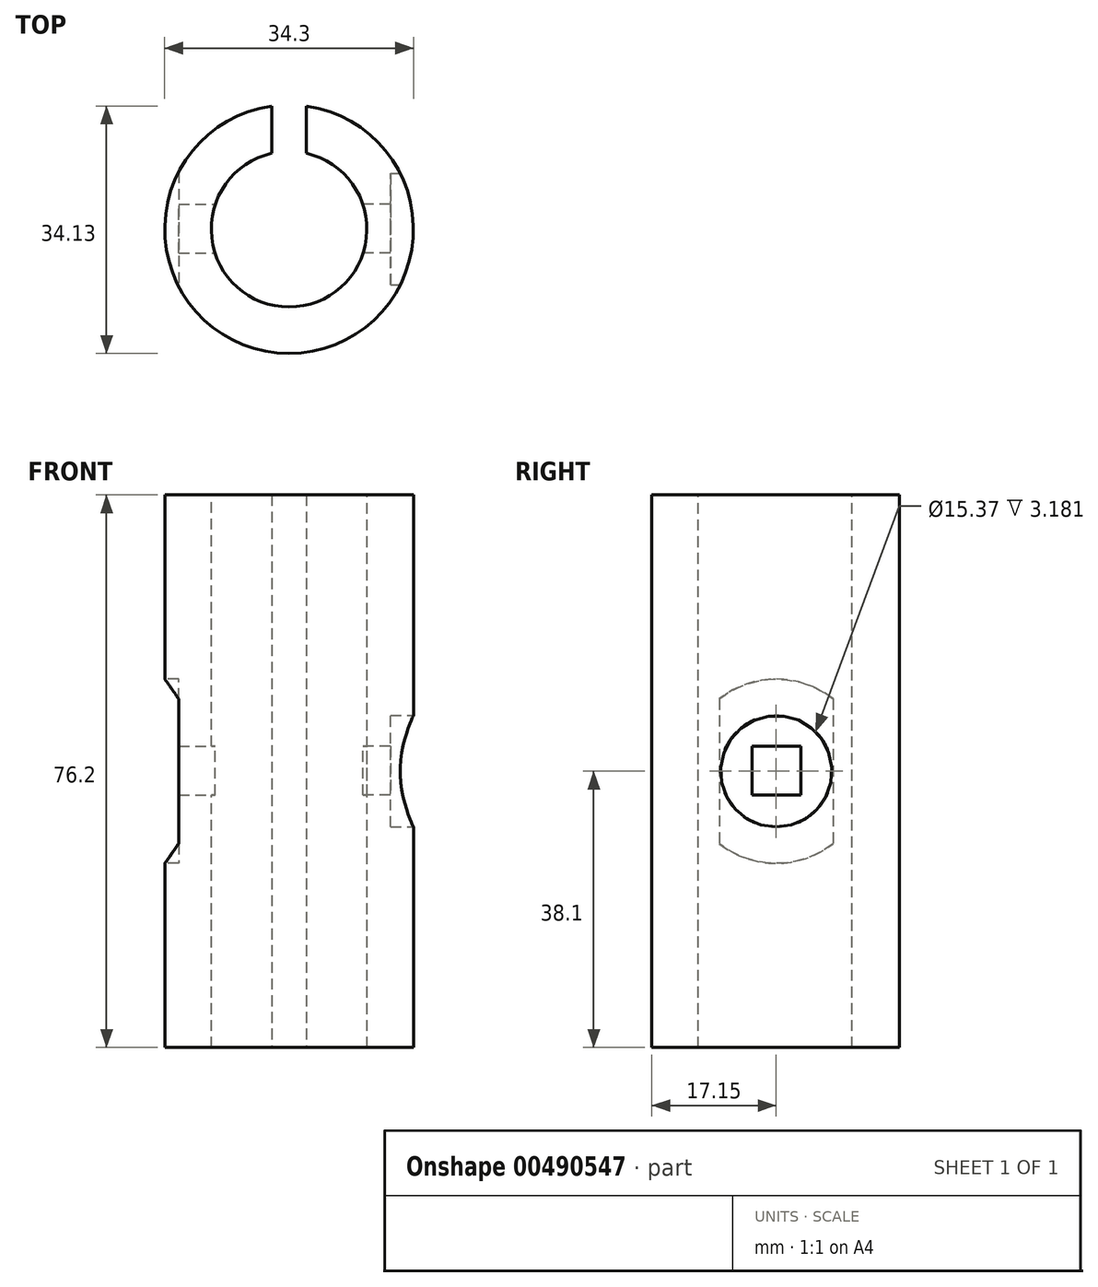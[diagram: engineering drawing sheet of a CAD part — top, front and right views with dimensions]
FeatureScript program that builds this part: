
annotation { "Feature Type Name" : "Feature", "Feature Type Description" : "" }
export const myFeature = defineFeature(function(context is Context, id is Id, definition is map)
    precondition{}
    {
        {
            var Q0;
            Q0=qCreatedBy(makeId("Top.planeOp"),FACE);
            var sketch = newSketch(context, id + "F0", { "sketchPlane" : qUnion([Q0])});
            skCircle(sketch, "E0", {"center": v(0, 0) * mm, "radius": 17.15 * mm});
            skSolve(sketch);
        }
        {
            var Q0;
            Q0 = qSketchRegion(id + "F0", true);
            extrude(context, id + "F1", {"entities" : qUnion([Q0]), "depth" : 76.2 * mm});
        }
        {
            var Q0;
            Q0=makeQuery(id+"F1.opExtrude","CAP_FACE",FACE,{"disambiguationData":[OSD([sQuery(id+"F0.wireOp",EDGE,"E0")])],"isStart":false});
            var sketch = newSketch(context, id + "F2", { "sketchPlane" : qUnion([Q0])});
            skCircle(sketch, "E1", {"center": v(0, 0) * mm, "radius": 10.73 * mm});
            skSolve(sketch);
        }
        {
            var Q0;
            Q0 = qSketchRegion(id + "F2", true);
            var Q1;
            Q1=makeQuery(id+"F2.imprint","IMPRINT",FACE,{"disambiguationData":[TD([[makeQuery(id+"F2.imprint","IMPRINT",EDGE,{"derivedFrom":sQuery(id+"F2.wireOp",EDGE,"E1")}),1.0]])]});
            extrude(context, id + "F3", {"entities" : qUnion([Q0, Q1]), "operationType" : NewBodyOperationType.REMOVE, "endBound" : BoundingType.THROUGH_ALL, "oppositeDirection" : true, "depth" : 25.4 * mm});
        }
        {
            var Q0;
            Q0=qCreatedBy(makeId("Right.planeOp"),FACE);
            var sketch = newSketch(context, id + "F4", { "sketchPlane" : qUnion([Q0])});
            skLineSegment(sketch, "E2.bottom", {"start": v(3.43, 41.53) * mm, "end": v(-3.3, 41.53) * mm});
            skLineSegment(sketch, "E2.top", {"start": v(3.43, 34.8) * mm, "end": v(-3.3, 34.8) * mm});
            skLineSegment(sketch, "E2.left", {"start": v(3.43, 41.53) * mm, "end": v(3.43, 34.8) * mm});
            skLineSegment(sketch, "E2.right", {"start": v(-3.3, 41.53) * mm, "end": v(-3.3, 34.8) * mm});
            skSolve(sketch);
        }
        {
            var Q0;
            Q0 = qSketchRegion(id + "F4", true);
            extrude(context, id + "F5", {"entities" : qUnion([Q0]), "operationType" : NewBodyOperationType.REMOVE, "endBound" : BoundingType.THROUGH_ALL, "oppositeDirection" : true, "depth" : 50.8 * mm});
        }
        {
            var Q0;
            Q0 = qSketchRegion(id + "F4", true);
            extrude(context, id + "F6", {"entities" : qUnion([Q0]), "operationType" : NewBodyOperationType.REMOVE, "endBound" : BoundingType.THROUGH_ALL, "depth" : 25.4 * mm});
        }
        {
            var Q0;
            Q0=qCreatedBy(makeId("Front.planeOp"),FACE);
            var sketch = newSketch(context, id + "F7", { "sketchPlane" : qUnion([Q0])});
            skLineSegment(sketch, "E3.bottom", {"start": v(-2.38, -5.2) * mm, "end": v(2.38, -5.2) * mm});
            skLineSegment(sketch, "E3.top", {"start": v(-2.38, 81.33) * mm, "end": v(2.38, 81.33) * mm});
            skLineSegment(sketch, "E3.left", {"start": v(-2.38, -5.2) * mm, "end": v(-2.38, 81.33) * mm});
            skLineSegment(sketch, "E3.right", {"start": v(2.38, -5.2) * mm, "end": v(2.38, 81.33) * mm});
            skLineSegment(sketch, "E4.bottom", {"start": v(0, 0) * mm, "end": v(2.38, 0) * mm});
            skLineSegment(sketch, "E4.top", {"start": v(0, -5.2) * mm, "end": v(2.38, -5.2) * mm});
            skLineSegment(sketch, "E4.left", {"start": v(0, 0) * mm, "end": v(0, -5.2) * mm});
            skLineSegment(sketch, "E4.right", {"start": v(2.38, 0) * mm, "end": v(2.38, -5.2) * mm});
            skSolve(sketch);
        }
        {
            var Q0;
            Q0 = qSketchRegion(id + "F7", true);
            extrude(context, id + "F8", {"entities" : qUnion([Q0]), "operationType" : NewBodyOperationType.REMOVE, "endBound" : BoundingType.THROUGH_ALL, "oppositeDirection" : true, "depth" : 25.4 * mm});
        }
        {
            var Q0;
            Q0=qCreatedBy(makeId("Right.planeOp"),FACE);
            cPlane(context, id + "F9", {"entities" : qUnion([Q0]), "cplaneType" : CPlaneType.OFFSET, "offset" : 25.4 * mm, "width" : 152.4 * mm, "height" : 152.4 * mm});
        }
        {
            var Q0;
            Q0=qCreatedBy(id+"F9.planeOp",FACE);
            var sketch = newSketch(context, id + "F10", { "sketchPlane" : qUnion([Q0])});
            skCircle(sketch, "E5", {"center": v(0, 38.1) * mm, "radius": 7.68 * mm});
            skSolve(sketch);
        }
        {
            var Q0;
            Q0 = qSketchRegion(id + "F10", true);
            extrude(context, id + "F11", {"entities" : qUnion([Q0]), "operationType" : NewBodyOperationType.REMOVE, "oppositeDirection" : true, "depth" : 11.43 * mm});
        }
        {
            var Q0;
            Q0=qCreatedBy(makeId("Right.planeOp"),FACE);
            cPlane(context, id + "F12", {"entities" : qUnion([Q0]), "cplaneType" : CPlaneType.OFFSET, "offset" : 25.4 * mm, "oppositeDirection" : true, "width" : 152.4 * mm, "height" : 152.4 * mm});
        }
        {
            var Q0;
            Q0=qCreatedBy(id+"F12.planeOp",FACE);
            var sketch = newSketch(context, id + "F13", { "sketchPlane" : qUnion([Q0])});
            skCircle(sketch, "E6", {"center": v(0, 38.1) * mm, "radius": 12.7 * mm});
            skSolve(sketch);
        }
        {
            var Q0;
            Q0 = qSketchRegion(id + "F13", true);
            extrude(context, id + "F14", {"entities" : qUnion([Q0]), "operationType" : NewBodyOperationType.REMOVE, "depth" : 10.16 * mm});
        }
    });
